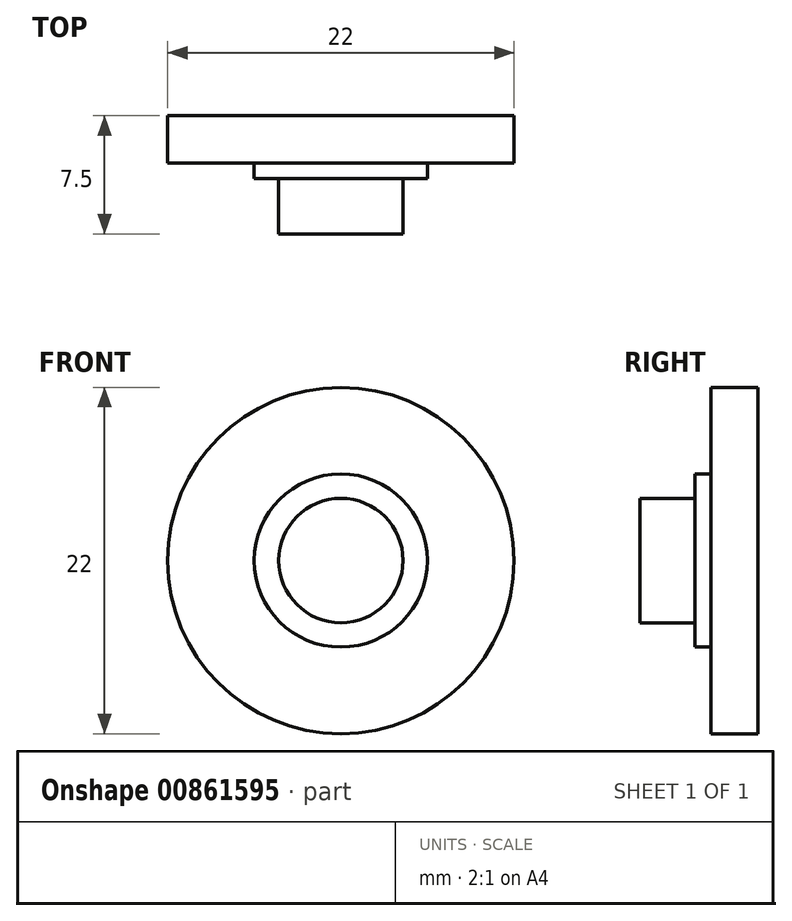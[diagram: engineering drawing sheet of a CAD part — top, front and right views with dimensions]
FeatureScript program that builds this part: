
annotation { "Feature Type Name" : "Feature", "Feature Type Description" : "" }
export const myFeature = defineFeature(function(context is Context, id is Id, definition is map)
    precondition{}
    {
        {
            var Q0;
            Q0=qCreatedBy(makeId("Top.planeOp"),FACE);
            var sketch = newSketch(context, id + "F0", { "sketchPlane" : qUnion([Q0])});
            skLineSegment(sketch, "E0", {"start": v(0, 0) * mm, "end": v(0, -7.5) * mm});
            skLineSegment(sketch, "E1", {"start": v(0, -7.5) * mm, "end": v(-3.95, -7.5) * mm});
            skLineSegment(sketch, "E2", {"start": v(-3.95, -7.5) * mm, "end": v(-3.95, -4) * mm});
            skLineSegment(sketch, "E3", {"start": v(-3.95, -4) * mm, "end": v(-5.5, -4) * mm});
            skLineSegment(sketch, "E4", {"start": v(-5.5, -4) * mm, "end": v(-5.5, -3) * mm});
            skLineSegment(sketch, "E5", {"start": v(-5.5, -3) * mm, "end": v(-11, -3) * mm});
            skLineSegment(sketch, "E6", {"start": v(-11, -3) * mm, "end": v(-11, 0) * mm});
            skLineSegment(sketch, "E7", {"start": v(-11, 0) * mm, "end": v(0, 0) * mm});
            skSolve(sketch);
        }
        {
            var Q0;
            Q0=makeQuery(id+"F0.imprint","IMPRINT",FACE,{"disambiguationData":[TD([[makeQuery(id+"F0.imprint","IMPRINT",EDGE,{"derivedFrom":sQuery(id+"F0.wireOp",EDGE,"E0")}),-1.0]])]});
            var Q1;
            Q1=sQuery(id+"F0.wireOp",EDGE,"E0");
            revolve(context, id + "F1", {"surfaceOperationType" : NewSurfaceOperationType.NEW, "entities" : qUnion([Q0]), "axis" : qUnion([Q1]), "revolveType" : RevolveType.FULL});
        }
    });
